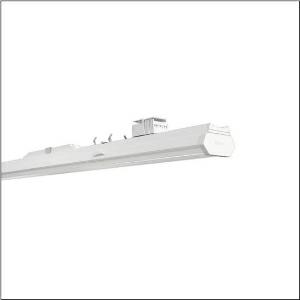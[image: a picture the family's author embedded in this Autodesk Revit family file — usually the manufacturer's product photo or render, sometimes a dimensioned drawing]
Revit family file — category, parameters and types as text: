
# Revit family: licross_21_protected_ho_52tp12dn4e5m3s4
name_source: partatom
category: Lighting Fixtures
units: mm (PartAtom-declared; Revit-internal decimal feet)

## family parameters
Cut with Voids When Loaded = No
Host = Face
Light Source = No
Part Type = Normal
Room Calculation Point = No
Round Connector Dimension = Use Diameter
Shared = No

## types (1)
- --- (1 x LED, 910 lm, 7.6 W, 4000K)
    Apparent Load = 8 VA
    CIE Flux Codes = 70 91 97 98 100
    Color Rendering = 80
    Color Temperature = 4000K
    Default Elevation = 1800 mm
    Description = Licross 21 Protected HO, luminaire insert, of sheet steel, galvanised, coil coated, white, length: 1.500mm, width: 90mm, height: 103mm, LED rated luminous flux: 14.690lm, light colour: 840, SDCM (Standard Deviation of Colour Matching)MacAdam ≤ 3 SDCM (initial), control gear: DALI 2, with plug, 6-pole, with phase selection, for trunking rail, 9 or 11-core, mains connection: 220..240V, AC, 50/60Hz, rated input power: 89W, for trunking rail, 9-/11-core, internal wiring halogen-free, for emergency light function, converter,control gear: single battery element, battery: LiFePO4, 9Ah, primary light control with lens, of plastic, primary optical cover: cover, of PMMA, light emission: direct distribution, primary light characteristic: symmetric, protection rating (complete): IP64, insulation class (complete): insulation class I (protective earthing), certification: CE, UKCA, protection symbol: D if used in an environment with conductive dust loads with corresponding accessories, impact resistance: IK06, permissible ambient temperature for indoor applications: +5..+30°C, standard: EN 60598-2-22, LABS conformity tested according to VDMA 24364:2018-05, reducing of maximum allowable ambient temperature of 5°C with ceiling mounting, corresponds to IFS (International Featured Standards) requirements for safety and quality in the food industry, The light source and the operating device comply with the requirements of the Ecodesign Regulation (EU) 2019/2020 and are replaceable in accordance with this regulation, packaging unit: 1 piece
    Height = 92 mm
    Lamp = 1 x LED
    Lamp Light Flux = 910 lm
    Lamp Power = 7.6 W
    Lamp count = 1
    Length = 1500 mm
    Luminous efficacy = 120 lm/W
    Manufacturer = Siteco
    ModVariant = No
    Model = 52TP12DN4E5M3S4
    Mounting Place = Ceiling
    Mounting Type = Pendant
    Number of Poles = 1
    OnlyDefault = Yes
    Power Factor = 1
    Product Name = Licross 21 Protected HO
    Product group = luminaire insert | ceiling pendant
    ProductGroupID = 901
    Protection Class = Protection class I
    Protection Degree = IP 64
    RLX_Detail_Level = 1
    RLX_Emergency_Light_Flux = 0 lm
    RLX_Emergency_Type = 0
    RLX_Emergency_Type_DB = No
    RlxData = <blob elided: 25149 chars, md5=f3e3f1f0>
    Socket = socket
    Standby Power = 0 W
    System Light Flux = 910 lm
    System Power = 8 W
    Type Comments = : emergency light operation: 3 h
    Type Image = l_1256148.jpg
    URL = http://relux.com
    VarID = @adj_111169
    Voltage = 0 V
    Weight = 0.00 kg
    Width = 88 mm

## geometry (parser evidence)
native form markers: Blend x4, Sweep x9
no freeform markers — native parametric forms only
